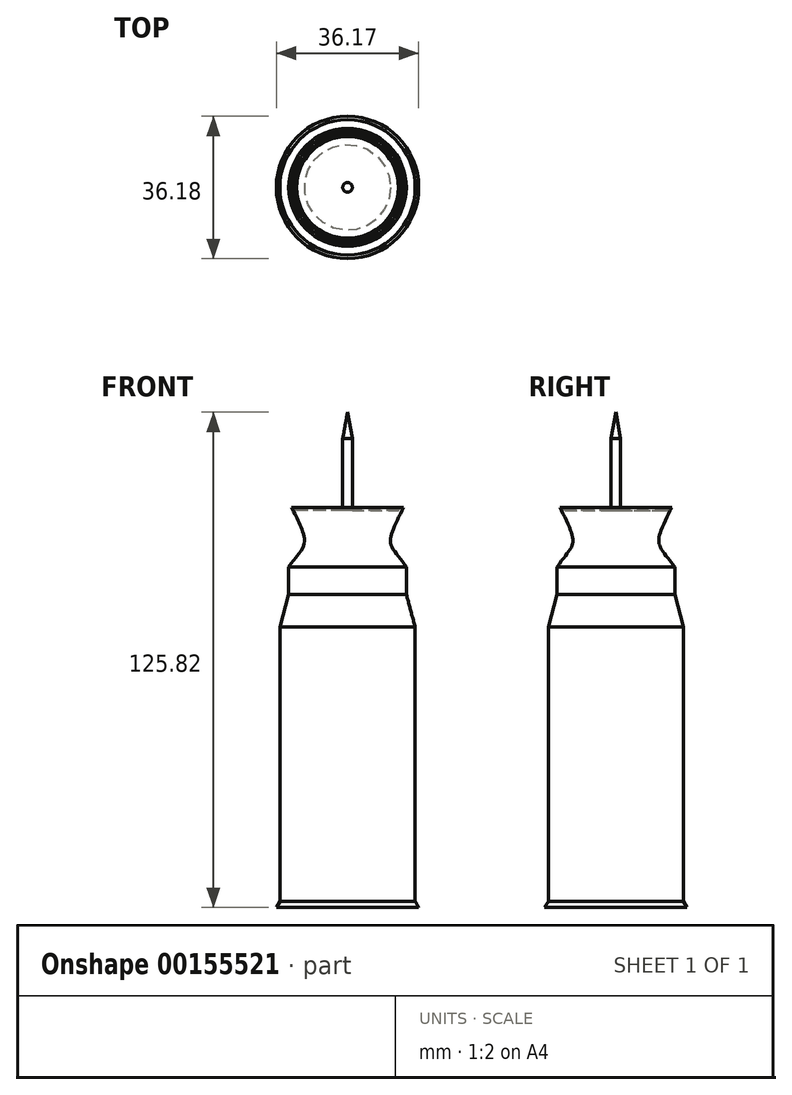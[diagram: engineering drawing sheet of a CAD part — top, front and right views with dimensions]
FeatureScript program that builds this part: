
annotation { "Feature Type Name" : "Feature", "Feature Type Description" : "" }
export const myFeature = defineFeature(function(context is Context, id is Id, definition is map)
    precondition{}
    {
        {
            var Q0;
            Q0=qCreatedBy(makeId("Front.planeOp"),FACE);
            var sketch = newSketch(context, id + "F0", { "sketchPlane" : qUnion([Q0])});
            skLineSegment(sketch, "E0", {"start": v(-42.7, 63.48) * mm, "end": v(-42.7, -62.34) * mm});
            skLineSegment(sketch, "E1", {"start": v(-25.78, -60.8) * mm, "end": v(-25.78, 8.86) * mm});
            skLineSegment(sketch, "E2", {"start": v(-25.78, 8.86) * mm, "end": v(-28.02, 17.14) * mm});
            skLineSegment(sketch, "E3", {"start": v(-28.02, 17.14) * mm, "end": v(-28.02, 24.12) * mm});
            skFitSpline(sketch, "E4", {"points": [v(-28.77, 39.37) * mm, v(-31.72, 32.5) * mm, v(-31.72, 29.31) * mm, v(-28.02, 24.12) * mm], "startDerivative": vector(-8.61, -19.2) * mm, "endDerivative": vector(9.39, -15.76) * mm});
            skLineSegment(sketch, "E5", {"start": v(-41.49, 56.76) * mm, "end": v(-42.7, 63.48) * mm});
            skLineSegment(sketch, "E6", {"start": v(-25.78, -60.8) * mm, "end": v(-24.93, -62.34) * mm});
            skLineSegment(sketch, "E7", {"start": v(-42.7, -62.34) * mm, "end": v(-24.93, -62.34) * mm});
            skLineSegment(sketch, "E8", {"start": v(-28.77, 39.37) * mm, "end": v(-29.53, 39.37) * mm});
            skLineSegment(sketch, "E9", {"start": v(-29.53, 39.37) * mm, "end": v(-30.01, 38.45) * mm});
            skLineSegment(sketch, "E10", {"start": v(-30.01, 38.45) * mm, "end": v(-41.43, 38.45) * mm});
            skLineSegment(sketch, "E11", {"start": v(-42.7, -62.34) * mm, "end": v(-60.78, -62.34) * mm});
            skLineSegment(sketch, "E12", {"start": v(-59.88, -60.8) * mm, "end": v(-59.88, 8.86) * mm});
            skLineSegment(sketch, "E13", {"start": v(-57.64, 17.14) * mm, "end": v(-59.88, 8.86) * mm});
            skLineSegment(sketch, "E14", {"start": v(-57.64, 17.14) * mm, "end": v(-57.64, 24.12) * mm});
            skFitSpline(sketch, "E15", {"points": [v(-56.9, 39.3) * mm, v(-53.92, 32.58) * mm, v(-53.93, 29.31) * mm, v(-57.64, 24.12) * mm], "startDerivative": vector(9.36, -19.16) * mm, "endDerivative": vector(-10.23, -15.63) * mm});
            skLineSegment(sketch, "E16", {"start": v(-43.92, 38.46) * mm, "end": v(-43.92, 56.76) * mm});
            skLineSegment(sketch, "E17", {"start": v(-43.92, 56.76) * mm, "end": v(-42.7, 63.48) * mm});
            skLineSegment(sketch, "E18", {"start": v(-59.88, -60.8) * mm, "end": v(-60.78, -62.34) * mm});
            skLineSegment(sketch, "E19", {"start": v(-56.9, 39.3) * mm, "end": v(-56.15, 39.3) * mm});
            skLineSegment(sketch, "E20", {"start": v(-55.63, 38.45) * mm, "end": v(-56.15, 39.3) * mm});
            skLineSegment(sketch, "E21", {"start": v(-55.63, 38.45) * mm, "end": v(-43.92, 38.46) * mm});
            skLineSegment(sketch, "E22", {"start": v(-41.49, 56.76) * mm, "end": v(-41.43, 38.45) * mm});
            skSolve(sketch);
        }
        {
            var Q0;
            Q0=makeQuery(id+"F0.imprint","IMPRINT",FACE,{"disambiguationData":[TD([[makeQuery(id+"F0.imprint","IMPRINT",EDGE,{"derivedFrom":sQuery(id+"F0.wireOp",EDGE,"E0")}),-1.0]])]});
            var Q1;
            Q1=sQuery(id+"F0.wireOp",EDGE,"E0");
            revolve(context, id + "F1", {"entities" : qUnion([Q0]), "axis" : qUnion([Q1]), "revolveType" : RevolveType.FULL});
        }
    });
